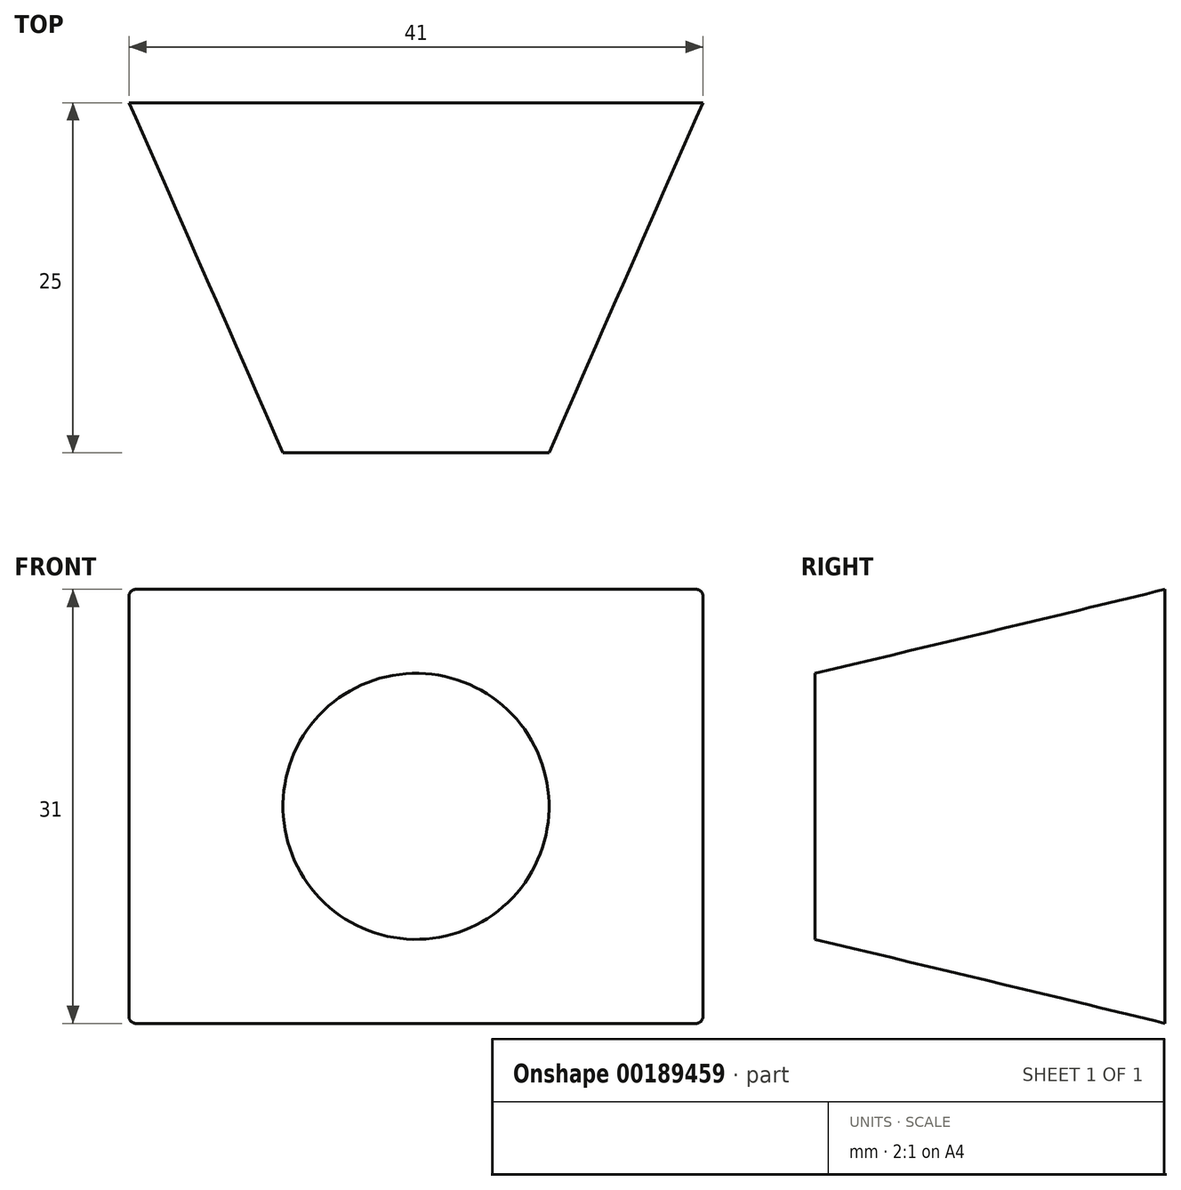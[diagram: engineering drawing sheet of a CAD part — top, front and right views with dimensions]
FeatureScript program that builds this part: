
annotation { "Feature Type Name" : "Feature", "Feature Type Description" : "" }
export const myFeature = defineFeature(function(context is Context, id is Id, definition is map)
    precondition{}
    {
        {
            var Q0;
            Q0=qCreatedBy(makeId("Front.planeOp"),FACE);
            var sketch = newSketch(context, id + "F0", { "sketchPlane" : qUnion([Q0])});
            skLineSegment(sketch, "E0.bottom", {"start": v(20, -15.5) * mm, "end": v(-20, -15.5) * mm});
            skLineSegment(sketch, "E0.top", {"start": v(20, 15.5) * mm, "end": v(-20, 15.5) * mm});
            skLineSegment(sketch, "E0.left", {"start": v(20.5, -15) * mm, "end": v(20.5, 15) * mm});
            skLineSegment(sketch, "E0.right", {"start": v(-20.5, -15) * mm, "end": v(-20.5, 15) * mm});
            skPoint(sketch, "E0.middle", {"position": v(0, 0) * mm});
            skLineSegment(sketch, "E1.0", {"start": v(21.5, -17.5) * mm, "end": v(-21.5, -17.5) * mm});
            skLineSegment(sketch, "E1.1", {"start": v(22.5, -16.5) * mm, "end": v(22.5, 16.5) * mm});
            skLineSegment(sketch, "E1.2", {"start": v(21.5, 17.5) * mm, "end": v(-21.5, 17.5) * mm});
            skLineSegment(sketch, "E1.3", {"start": v(-22.5, -16.5) * mm, "end": v(-22.5, 16.5) * mm});
            skPoint(sketch, "E2.visualSharp", {"position": v(-20.5, 15.5) * mm});
            skArc(sketch, "E2.filletArc", {"start": v(-20, 15.5) * mm, "mid": v(-20.35, 15.35) * mm, "end": v(-20.5, 15) * mm});
            skPoint(sketch, "E3.visualSharp", {"position": v(20.5, 15.5) * mm});
            skArc(sketch, "E3.filletArc", {"start": v(20.5, 15) * mm, "mid": v(20.35, 15.35) * mm, "end": v(20, 15.5) * mm});
            skPoint(sketch, "E4.visualSharp", {"position": v(20.5, -15.5) * mm});
            skArc(sketch, "E4.filletArc", {"start": v(20, -15.5) * mm, "mid": v(20.35, -15.35) * mm, "end": v(20.5, -15) * mm});
            skPoint(sketch, "E5.visualSharp", {"position": v(-20.5, -15.5) * mm});
            skArc(sketch, "E5.filletArc", {"start": v(-20.5, -15) * mm, "mid": v(-20.35, -15.35) * mm, "end": v(-20, -15.5) * mm});
            skPoint(sketch, "E6.visualSharp", {"position": v(-22.5, 17.5) * mm});
            skArc(sketch, "E6.filletArc", {"start": v(-21.5, 17.5) * mm, "mid": v(-22.2, 17.2) * mm, "end": v(-22.5, 16.5) * mm});
            skPoint(sketch, "E7.visualSharp", {"position": v(22.5, 17.5) * mm});
            skArc(sketch, "E7.filletArc", {"start": v(22.5, 16.5) * mm, "mid": v(22.2, 17.2) * mm, "end": v(21.5, 17.5) * mm});
            skPoint(sketch, "E8.visualSharp", {"position": v(22.5, -17.5) * mm});
            skArc(sketch, "E8.filletArc", {"start": v(21.5, -17.5) * mm, "mid": v(22.2, -17.2) * mm, "end": v(22.5, -16.5) * mm});
            skPoint(sketch, "E9.visualSharp", {"position": v(-22.5, -17.5) * mm});
            skArc(sketch, "E9.filletArc", {"start": v(-22.5, -16.5) * mm, "mid": v(-22.2, -17.2) * mm, "end": v(-21.5, -17.5) * mm});
            skSolve(sketch);
        }
        {
            var Q0;
            Q0=qCreatedBy(makeId("Front.planeOp"),FACE);
            cPlane(context, id + "F1", {"entities" : qUnion([Q0]), "cplaneType" : CPlaneType.OFFSET, "offset" : 25 * mm, "width" : 150 * mm, "height" : 150 * mm});
        }
        {
            var Q0;
            Q0=qCreatedBy(id+"F1.planeOp",FACE);
            var sketch = newSketch(context, id + "F2", { "sketchPlane" : qUnion([Q0])});
            skCircle(sketch, "E10", {"center": v(0, 0) * mm, "radius": 10.5 * mm});
            skCircle(sketch, "E11", {"center": v(0, 0) * mm, "radius": 9.5 * mm});
            skSolve(sketch);
        }
        {
            var Q0;
            Q0=makeQuery(id+"F0.imprint","IMPRINT",FACE,{"disambiguationData":[TD([[makeQuery(id+"F0.imprint","IMPRINT",EDGE,{"derivedFrom":sQuery(id+"F0.wireOp",EDGE,"E0.bottom")}),-1.0]])]});
            var Q1;
            Q1=makeQuery(id+"F2.imprint","IMPRINT",FACE,{"disambiguationData":[TD([[makeQuery(id+"F2.imprint","IMPRINT",EDGE,{"derivedFrom":sQuery(id+"F2.wireOp",EDGE,"E11")}),1.0]])]});
            var Q2;
            Q2=sQuery(id+"F0.wireOp",EDGE,"E0.bottom");
            loft(context, id + "F3", {"sheetProfilesArray" : [{ "sheetProfileEntities" : qUnion([Q0]) }, { "sheetProfileEntities" : qUnion([Q1]) }], "wireProfilesArray" : [{ "wireProfileEntities" : qUnion([Q2]) }]});
        }
    });
